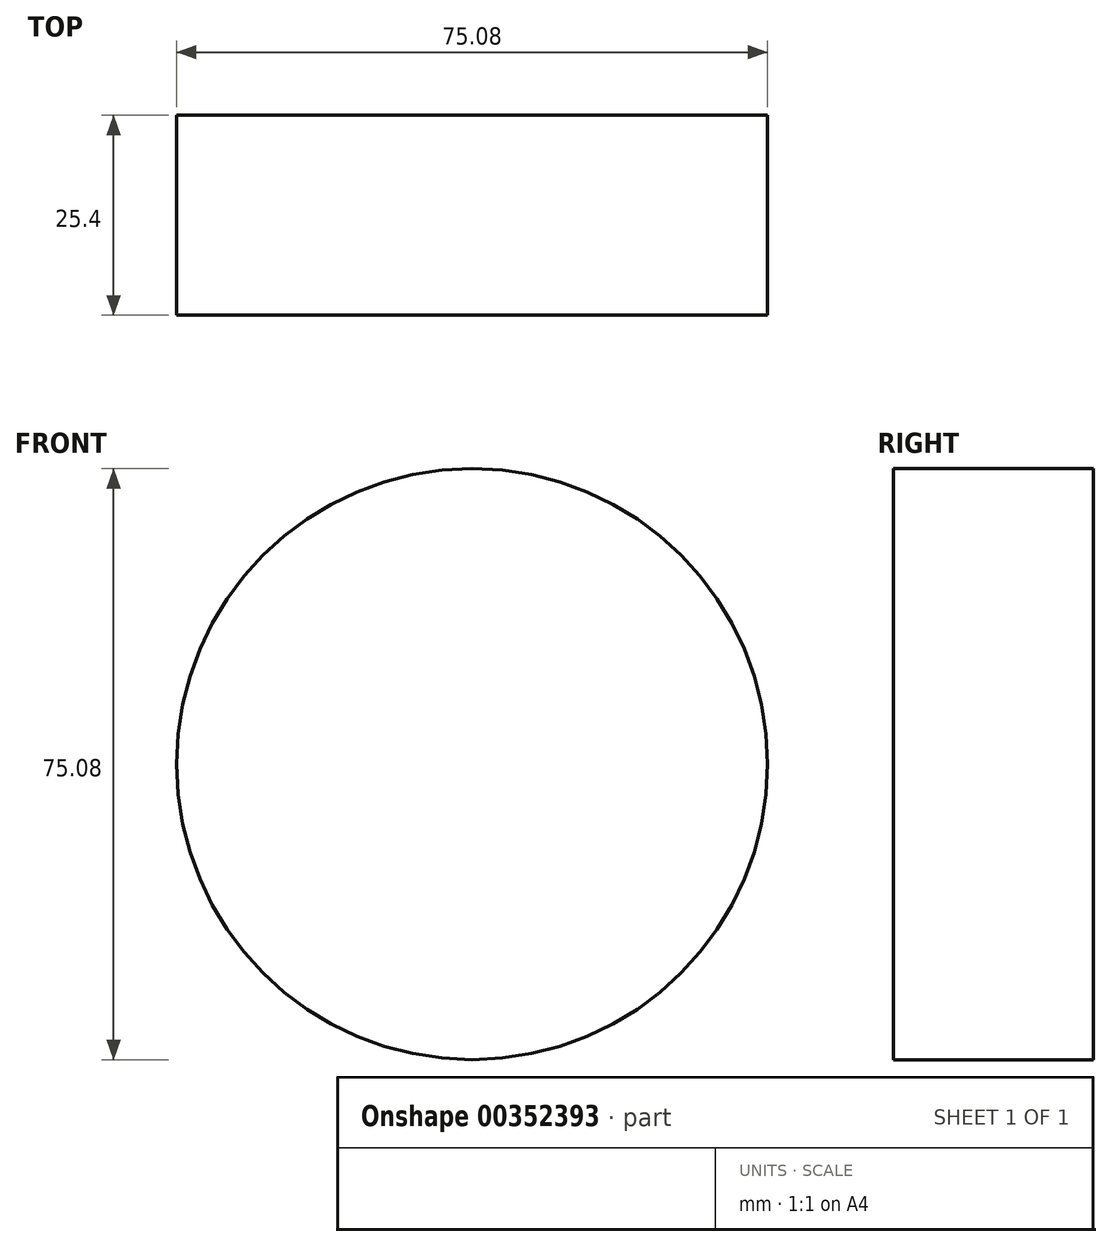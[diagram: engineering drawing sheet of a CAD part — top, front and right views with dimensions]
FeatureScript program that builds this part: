
annotation { "Feature Type Name" : "Feature", "Feature Type Description" : "" }
export const myFeature = defineFeature(function(context is Context, id is Id, definition is map)
    precondition{}
    {
        {
            var Q0;
            Q0=qCreatedBy(makeId("Front.planeOp"),FACE);
            var sketch = newSketch(context, id + "F0", { "sketchPlane" : qUnion([Q0])});
            skCircle(sketch, "E0", {"center": v(0, 0) * mm, "radius": 37.54 * mm});
            skSolve(sketch);
        }
        {
            var Q0;
            Q0=makeQuery(id+"F0.imprint","IMPRINT",FACE,{"disambiguationData":[TD([[makeQuery(id+"F0.imprint","IMPRINT",EDGE,{"derivedFrom":sQuery(id+"F0.wireOp",EDGE,"E0")}),1.0]])]});
            extrude(context, id + "F1", {"entities" : qUnion([Q0]), "depth" : 25.4 * mm});
        }
    });
